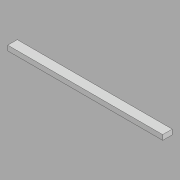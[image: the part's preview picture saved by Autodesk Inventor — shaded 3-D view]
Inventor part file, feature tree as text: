
AUTODESK INVENTOR PART (.ipt)
format: ipt  version: 2022.2 (Build 262287010, 287A)  size: 105,472 bytes
history: native  units: in
note: dims shown in document units (in); Inventor stores cm internally (conversion verified against a paired STEP export)
features: direct_edit x1, other x1, revolve x1
ambient origin geometry x8: Origin, YZ Plane, XZ Plane, XY Plane, X Axis, Y Axis, Z Axis, Center Point
bodies: Solid1 (feature_tree)
feature tree (3):
  direct_edit  "Direct Edit1"
  other  "E125 & E137"
  revolve  "Rotate1"  Angle=90.0deg
